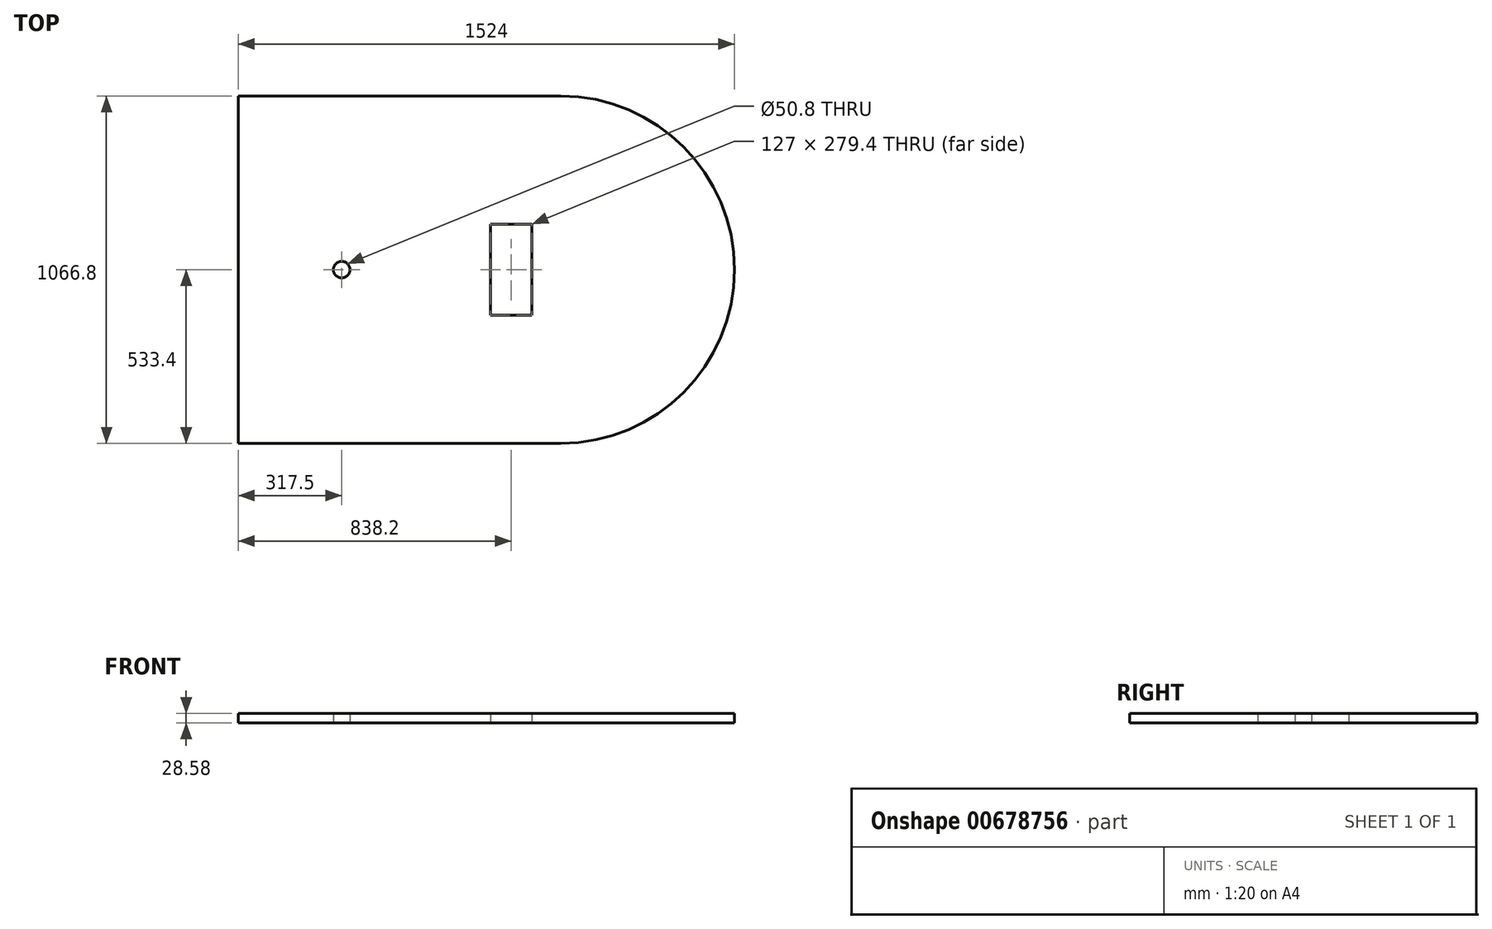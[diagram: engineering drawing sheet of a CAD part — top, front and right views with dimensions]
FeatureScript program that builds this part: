
annotation { "Feature Type Name" : "Feature", "Feature Type Description" : "" }
export const myFeature = defineFeature(function(context is Context, id is Id, definition is map)
    precondition{}
    {
        {
            var Q0;
            Q0=qCreatedBy(makeId("Top.planeOp"),FACE);
            var sketch = newSketch(context, id + "F0", { "sketchPlane" : qUnion([Q0])});
            skLineSegment(sketch, "E0.right", {"start": v(-1447.8, 533.4) * mm, "end": v(-1447.8, -533.4) * mm});
            skPoint(sketch, "E0.middle", {"position": v(0, 0) * mm});
            skPoint(sketch, "E1.endSnap0", {"position": v(1447.8, 0) * mm});
            skPoint(sketch, "E2.visualSharp", {"position": v(-1447.8, 533.4) * mm});
            skPoint(sketch, "E3.visualSharp", {"position": v(-1447.8, -533.4) * mm});
            skLineSegment(sketch, "E4", {"start": v(-1447.8, 0) * mm, "end": v(-1130.3, 0) * mm});
            skPoint(sketch, "E4.endSnap0", {"position": v(-1447.8, 0) * mm});
            skCircle(sketch, "E5", {"center": v(-1130.3, 0) * mm, "radius": 25.4 * mm});
            skLineSegment(sketch, "E6", {"start": v(-1447.8, -533.4) * mm, "end": v(-1447.8, -533.4) * mm});
            skLineSegment(sketch, "E7", {"start": v(-1371.6, -533.4) * mm, "end": v(-1447.8, -533.4) * mm});
            skLineSegment(sketch, "E8", {"start": v(-1447.8, 533.4) * mm, "end": v(-1447.8, 533.4) * mm});
            skLineSegment(sketch, "E9", {"start": v(-1371.6, 533.4) * mm, "end": v(-1447.8, 533.4) * mm});
            skLineSegment(sketch, "E10", {"start": v(-1447.8, -533.4) * mm, "end": v(-685.8, -533.4) * mm});
            skLineSegment(sketch, "E11", {"start": v(-1447.8, 533.4) * mm, "end": v(76.2, 533.4) * mm});
            skLineSegment(sketch, "E12", {"start": v(76.2, 533.4) * mm, "end": v(76.2, -533.4) * mm});
            skLineSegment(sketch, "E13", {"start": v(76.2, -533.4) * mm, "end": v(-1447.8, -533.4) * mm});
            skLineSegment(sketch, "E14", {"start": v(76.2, 533.4) * mm, "end": v(-457.2, 533.4) * mm});
            skLineSegment(sketch, "E15", {"start": v(-457.2, 533.4) * mm, "end": v(-457.2, 0) * mm});
            skArc(sketch, "E16", {"start": v(-457.2, 533.4) * mm, "mid": v(76.2, 0) * mm, "end": v(-457.2, -533.4) * mm});
            skLineSegment(sketch, "E17", {"start": v(-546.1, 0) * mm, "end": v(76.2, 0) * mm});
            skLineSegment(sketch, "E18", {"start": v(-546.1, 0) * mm, "end": v(-609.6, 0) * mm});
            skLineSegment(sketch, "E19.bottom", {"start": v(-546.1, 139.7) * mm, "end": v(-673.1, 139.7) * mm});
            skLineSegment(sketch, "E19.top", {"start": v(-546.1, -139.7) * mm, "end": v(-673.1, -139.7) * mm});
            skLineSegment(sketch, "E19.left", {"start": v(-546.1, 139.7) * mm, "end": v(-546.1, -139.7) * mm});
            skLineSegment(sketch, "E19.right", {"start": v(-673.1, 139.7) * mm, "end": v(-673.1, -139.7) * mm});
            skPoint(sketch, "E19.middle", {"position": v(-609.6, 0) * mm});
            skSolve(sketch);
        }
        {
            var Q0;
            Q0=makeQuery(id+"F0.imprint","IMPRINT",FACE,{"disambiguationData":[TD([[makeQuery(id+"F0.imprint","IMPRINT",EDGE,{"derivedFrom":sQuery(id+"F0.wireOp",EDGE,"E0.right")}),1.0]])]});
            var Q1;
            {var subQ0=sQuery(id+"F0.wireOp",EDGE,"E15");Q1=makeQuery(id+"F0.imprint","IMPRINT",FACE,{"disambiguationData":[TD([[makeQuery(id+"F0.imprint","IMPRINT",EDGE,{"derivedFrom":subQ0}),1.0]])]});}
            extrude(context, id + "F1", {"entities" : qUnion([Q0, Q1]), "depth" : 28.57 * mm, "offsetDistance" : 25.4 * mm});
        }
    });
